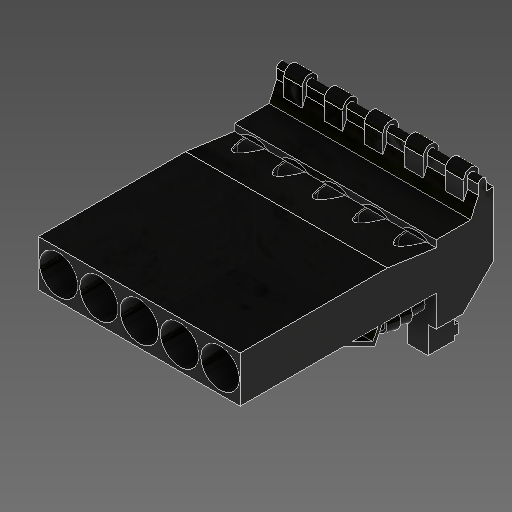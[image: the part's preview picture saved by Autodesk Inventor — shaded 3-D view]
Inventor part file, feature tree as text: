
AUTODESK INVENTOR PART (.ipt)
format: ipt  version: 2020 (Build 240168000, 168)  size: 775,168 bytes
history: native  units: in
note: dims shown in document units (in); Inventor stores cm internally (conversion verified against a paired STEP export)
features: other x15, extrude x15, fillet x3, chamfer x2, pattern_linear x1, sketch x1, projected_geometry x1
ambient origin geometry x8: Origin, YZ Plane, XZ Plane, XY Plane, X Axis, Y Axis, Z Axis, Center Point
bodies: Solid1 (feature_tree)
feature tree (38):
  other  "Base Sketch"
  extrude  "Side Walls"  TaperAngle=0.0deg  [1 undecoded]
  extrude  "Back Wall"  TaperAngle=0.0deg  [1 undecoded]
  extrude  "Front Wall"  TaperAngle=0.0deg  [1 undecoded]
  extrude  "Whistle Housing"  Depth=0.0157in TaperAngle=0.0deg
  extrude  "Tube Socket"  Depth=0.0157in
  other  "Midplane"
  extrude  "Slit"  Depth=0.0157in
  other  "Silicone Fitting"
  extrude  "Silicone Fitting to Chamber"  Depth=0.0157in
  extrude  "Hinge"  Depth=0.0157in
  extrude  "Hinge Nub"  TaperAngle=90.0deg  [1 undecoded]
  chamfer  "Hinge Clearance Chamfer"  Distance=1.5748in
  chamfer  "Spring Pass Chamfer"  Distance=0.3937in
  extrude  "Spring Block"  TaperAngle=0.0deg  [1 undecoded]
  extrude  "Spring Hook"  Depth=0.0157in
  other  "Sping Hook Draft"
  fillet  "Spring Hook Fillet"  Radius=0.4134in
  extrude  "Edge Cut"  TaperAngle=0.0deg  [1 undecoded]
  fillet  "Edge Fillet"  Radius=0.189in
  other  "Pincher Triangle Sketch"
  extrude  "Pincher Triangle"  TaperAngle=0.0deg  [1 undecoded]
  extrude  "Triangle Coupling Male"  Depth=0.0079in
  extrude  "Expand: Triangle Coupling Female"  Depth=0.0787in
  pattern_linear  "Key Repitition"  Spacing1=45.0deg  [1 undecoded]
  fillet  "Fillet: Triangle Coupling Male"  Radius=0.0787in
  sketch  "Sketch5"  dims[d1=0.0in d2=0.0in d3=0.0in d4=0.0in d61=1.5748in d62=0.0in d65=0.0938in d66=0.1181in d67=0.0276in d68=0.0197in d69=90.0deg d71=1.5748in d72=0.0in d78=0.3937in d80=0.0in d81=0.4331in d88=0.4134in d89=0.0in d92=0.189in d93=0.0in d101=0.0079in d105=0.0787in d106=0.1772in d107=45.0deg d112=0.0787in d113=45.0deg d135=0.2067in d136=0.315in d137=0.5906in d139=0.0in d160=0.1181in d161=0.0984in d162=0.3937in d163=0.1575in d164=0.0in d171=1.03in d173=0.4724in d176=0.4134in d177=0.0in d178=0.2067in d179=0.0in d180=0.1374in d181=0.0394in d187=0.2067in d188=0.2362in d190=0.5906in d191=0.0in d193=0.1654in d194=0.0512in d198=0.4134in d199=0.0in d277=0.0079in d278=1.9685in d280=0.4134in d282=0.4134in d283=0.0in d284=0.0394in d285=0.0079in d289=0.0827in d298=0.2067in d299=0.0in d300=0.315in d301=0.0079in d302=0.0394in d303=0.0787in d304=0.0157in]
  projected_geometry  "Projected Loop2"
  other  "Whistle Housing Sketch"
  other  "Edge Cut Sketch"
  other  "Slit Sketch"
  other  "Silicone Fitting Sketch"
  other  "Silicone Fitting to Chamber Sketch"
  other  "Tube Socket Sketch"
  other  "Hinge Sketch"
  other  "Hinge Nub Sketch"
  other  "Spring Block Sketch"
  other  "Spring Hook Sketch"
note: 8 required parameter values undecoded (feature->parameter linkage not recoverable at this tier; creation-order binding heuristic only, values carry confidence <= 0.55)
